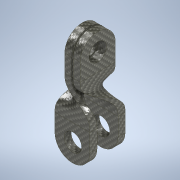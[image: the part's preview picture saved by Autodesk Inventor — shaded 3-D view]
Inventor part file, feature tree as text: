
AUTODESK INVENTOR PART (.ipt)
format: ipt  version: 2022 (Build 260153000, 153)  size: 304,640 bytes
history: native  units: mm
features: other x6, sketch x5, extrude x4, fillet x3, hole x2, loft x2, projected_geometry x1
ambient origin geometry x8: Origin, YZ Plane, XZ Plane, XY Plane, X Axis, Y Axis, Z Axis, Center Point
bodies: Body1 (feature_tree)
feature tree (23):
  other  "Těleso1"
  sketch  "Náčrt1"
  extrude  "Vysunutí1"  Depth=50.0mm
  extrude  "Vysunutí2"  Depth=10.0mm
  fillet  "Zaoblení1"  Radius=10.0mm
  fillet  "Zaoblení2"  Radius=2.0mm
  hole  "Díra1"  [1 undecoded]
  extrude  "Vysunutí3"  Depth=2.0mm
  other  "Pracovní rovina2"
  extrude  "Vysunutí4"  Depth=50.0mm TaperAngle=0.0deg
  fillet  "Zaoblení3"  Radius=46.0mm
  hole  "Díra2"  [1 undecoded]
  loft  "Šablonování1"
  loft  "Šablonování2"
  sketch  "Náčrt2"
  sketch  "Náčrt8"
  projected_geometry  "Promítnutá smyčka1"
  sketch  "Náčrt9"
  sketch  "Náčrt10"
  other  "Hrany1"
  other  "Hrany2"
  other  "Hrany3"
  other  "Hrany4"
note: 2 required parameter values undecoded (feature->parameter linkage not recoverable at this tier; creation-order binding heuristic only, values carry confidence <= 0.55)
